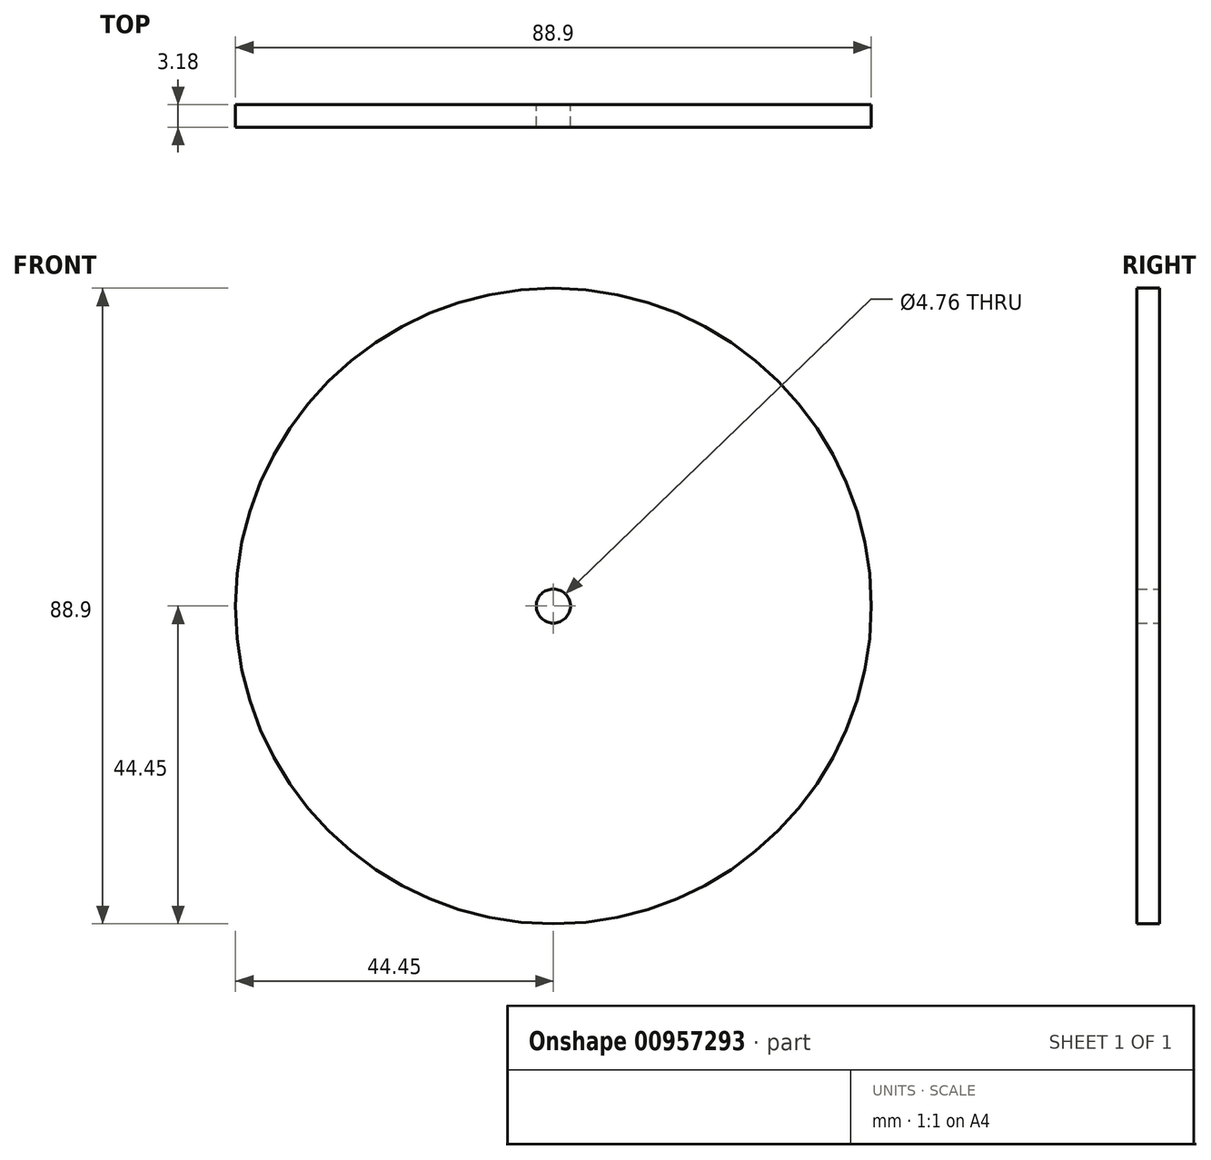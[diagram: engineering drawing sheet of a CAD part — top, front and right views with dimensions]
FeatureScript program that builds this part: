
annotation { "Feature Type Name" : "Feature", "Feature Type Description" : "" }
export const myFeature = defineFeature(function(context is Context, id is Id, definition is map)
    precondition{}
    {
        {
            var Q0;
            Q0=qCreatedBy(makeId("Front.planeOp"),FACE);
            var sketch = newSketch(context, id + "F0", { "sketchPlane" : qUnion([Q0])});
            skCircle(sketch, "E0", {"center": v(0, 0) * mm, "radius": 44.45 * mm});
            skCircle(sketch, "E1", {"center": v(0, 0) * mm, "radius": 2.38 * mm});
            skSolve(sketch);
        }
        {
            var Q0;
            Q0=makeQuery(id+"F0.imprint","IMPRINT",FACE,{"disambiguationData":[TD([[makeQuery(id+"F0.imprint","IMPRINT",EDGE,{"derivedFrom":sQuery(id+"F0.wireOp",EDGE,"E0")}),1.0]])]});
            extrude(context, id + "F1", {"entities" : qUnion([Q0]), "depth" : 3.17 * mm, "offsetDistance" : 25.4 * mm});
        }
    });
